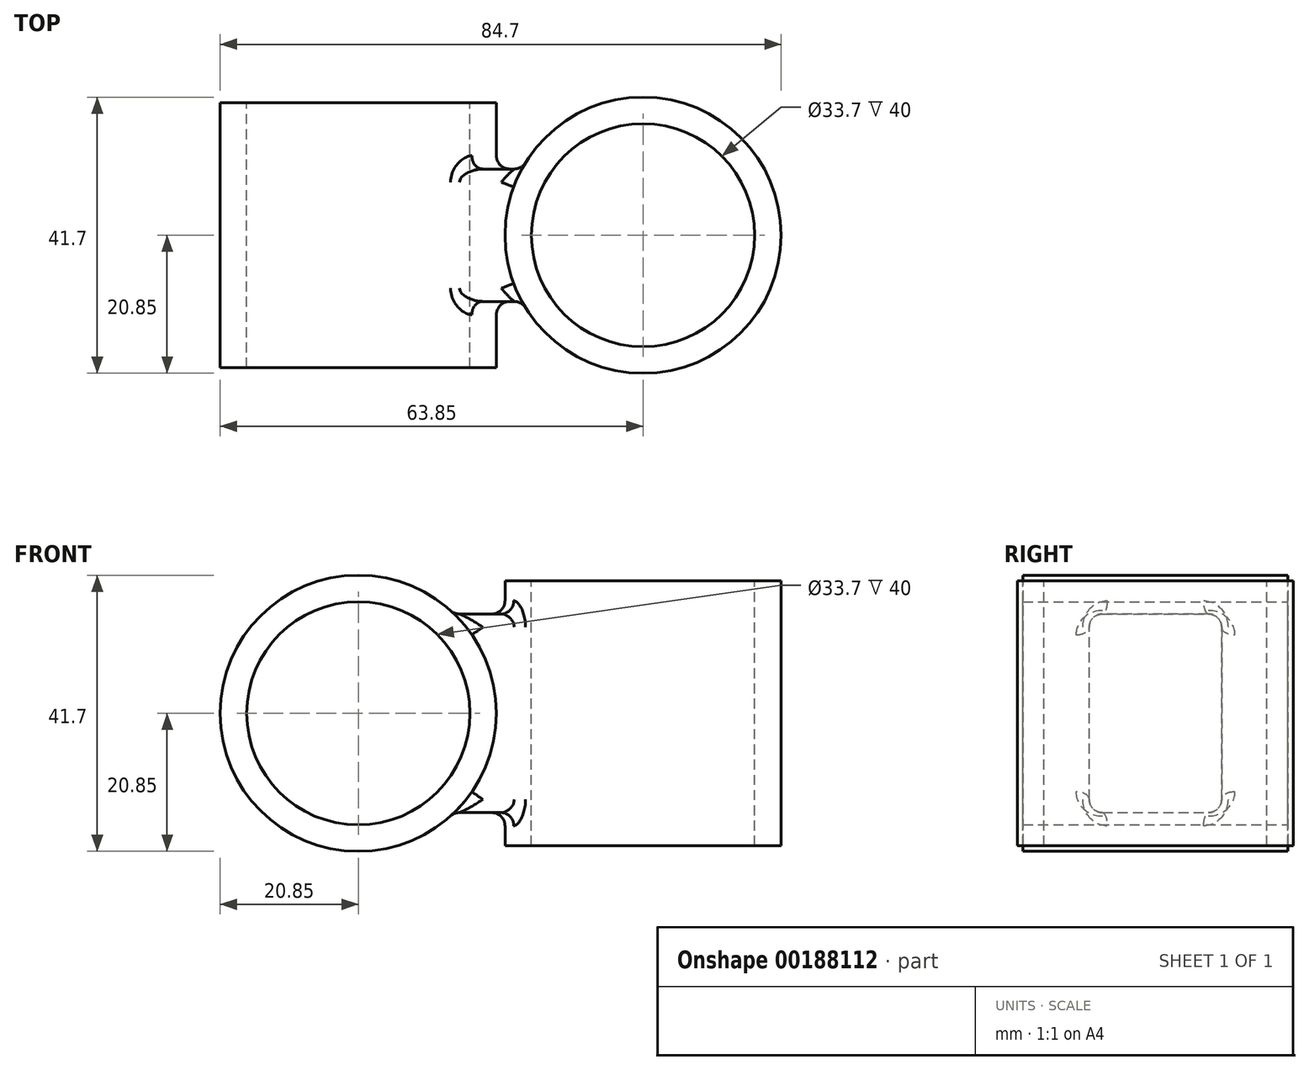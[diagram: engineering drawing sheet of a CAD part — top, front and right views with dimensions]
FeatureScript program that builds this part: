
annotation { "Feature Type Name" : "Feature", "Feature Type Description" : "" }
export const myFeature = defineFeature(function(context is Context, id is Id, definition is map)
    precondition{}
    {
        {
            var Q0;
            Q0=qCreatedBy(makeId("Front.planeOp"),FACE);
            var sketch = newSketch(context, id + "F0", { "sketchPlane" : qUnion([Q0])});
            skCircle(sketch, "E0", {"center": v(0, 0) * mm, "radius": 16.85 * mm});
            skCircle(sketch, "E1", {"center": v(0, 0) * mm, "radius": 20.85 * mm});
            skSolve(sketch);
        }
        {
            var Q0;
            Q0=makeQuery(id+"F0.imprint","IMPRINT",FACE,{"disambiguationData":[TD([[makeQuery(id+"F0.imprint","IMPRINT",EDGE,{"derivedFrom":sQuery(id+"F0.wireOp",EDGE,"E0")}),1.0]])]});
            extrude(context, id + "F1", {"entities" : qUnion([Q0]), "depth" : 40 * mm, "symmetric" : true});
        }
        {
            var Q0;
            Q0=makeQuery(id+"F0.imprint","IMPRINT",FACE,{"disambiguationData":[TD([[makeQuery(id+"F0.imprint","IMPRINT",EDGE,{"derivedFrom":sQuery(id+"F0.wireOp",EDGE,"E0")}),-1.0]])]});
            extrude(context, id + "F2", {"entities" : qUnion([Q0]), "depth" : 40 * mm, "symmetric" : true});
        }
        {
            var Q0;
            Q0=makeQuery(id+"F2.opExtrude","SWEPT_BODY",BODY,{"disambiguationData":[OSD([sQuery(id+"F0.wireOp",EDGE,"E0"),sQuery(id+"F0.wireOp",EDGE,"E1")])]});
            transform(context, id + "F3", {"entities" : qUnion([Q0]), "transformType" : TransformType.TRANSLATION_3D, "dx" : 43 * mm, "dy" : 0 * mm, "dz" : 0 * mm, "makeCopy" : true});
        }
        {
            var Q0;
            Q0=makeQuery(id+"F1.opExtrude","SWEPT_BODY",BODY,{"disambiguationData":[OSD([sQuery(id+"F0.wireOp",EDGE,"E0")])]});
            transform(context, id + "F4", {"entities" : qUnion([Q0]), "transformType" : TransformType.TRANSLATION_3D, "dx" : 43 * mm, "dy" : 0 * mm, "dz" : 0 * mm, "makeCopy" : true});
        }
        {
            var Q0;
            Q0=qCreatedBy(makeId("Front.planeOp"),FACE);
            var sketch = newSketch(context, id + "F5", { "sketchPlane" : qUnion([Q0])});
            skLineSegment(sketch, "E2.bottom", {"start": v(30.5, 15) * mm, "end": v(12.5, 15) * mm});
            skLineSegment(sketch, "E2.top", {"start": v(30.5, -15) * mm, "end": v(12.5, -15) * mm});
            skLineSegment(sketch, "E2.left", {"start": v(30.5, 15) * mm, "end": v(30.5, -15) * mm});
            skLineSegment(sketch, "E2.right", {"start": v(12.5, 15) * mm, "end": v(12.5, -15) * mm});
            skPoint(sketch, "E2.middle", {"position": v(21.5, 0) * mm});
            skLineSegment(sketch, "E3", {"start": v(14.35, 0) * mm, "end": v(26.07, 0) * mm});
            skSolve(sketch);
        }
        {
            var Q0;
            Q0=makeQuery(id+"F3.opPattern","COPY",BODY,{"derivedFrom":makeQuery(id+"F2.opExtrude","SWEPT_BODY",BODY,{"disambiguationData":[OSD([sQuery(id+"F0.wireOp",EDGE,"E0"),sQuery(id+"F0.wireOp",EDGE,"E1")])]}),"instanceName":"1"});
            var Q1;
            Q1=sQuery(id+"F5.wireOp",EDGE,"E3");
            transform(context, id + "F6", {"entities" : qUnion([Q0]), "transformType" : TransformType.ROTATION, "transformAxis" : qUnion([Q1]), "angle" : 90 * degree, "makeCopy" : false});
        }
        {
            var Q0;
            Q0=makeQuery(id+"F4.opPattern","COPY",BODY,{"derivedFrom":makeQuery(id+"F1.opExtrude","SWEPT_BODY",BODY,{"disambiguationData":[OSD([sQuery(id+"F0.wireOp",EDGE,"E0")])]}),"instanceName":"1"});
            var Q1;
            Q1=sQuery(id+"F5.wireOp",EDGE,"E3");
            transform(context, id + "F7", {"entities" : qUnion([Q0]), "transformType" : TransformType.ROTATION, "transformAxis" : qUnion([Q1]), "angle" : 90 * degree, "makeCopy" : false});
        }
        {
            var Q0;
            Q0=makeQuery(id+"F5.imprint","IMPRINT",FACE,{"disambiguationData":[TD([[makeQuery(id+"F5.imprint","IMPRINT",EDGE,{"derivedFrom":sQuery(id+"F5.wireOp",EDGE,"E2.bottom")}),1.0]])]});
            extrude(context, id + "F8", {"entities" : qUnion([Q0]), "depth" : 20 * mm, "symmetric" : true});
        }
        {
            var Q0;
            Q0=makeQuery(id+"F1.opExtrude","SWEPT_BODY",BODY,{"disambiguationData":[OSD([sQuery(id+"F0.wireOp",EDGE,"E0")])]});
            var Q1;
            Q1=makeQuery(id+"F4.opPattern","COPY",BODY,{"derivedFrom":makeQuery(id+"F1.opExtrude","SWEPT_BODY",BODY,{"disambiguationData":[OSD([sQuery(id+"F0.wireOp",EDGE,"E0")])]}),"instanceName":"1"});
            var Q2;
            Q2=makeQuery(id+"F8.opExtrude","SWEPT_BODY",BODY,{"disambiguationData":[OSD([sQuery(id+"F5.wireOp",EDGE,"E2.bottom"),sQuery(id+"F5.wireOp",EDGE,"E2.top"),sQuery(id+"F5.wireOp",EDGE,"E2.left"),sQuery(id+"F5.wireOp",EDGE,"E2.right")])]});
            booleanBodies(context, id + "F9", {"operationType" : BooleanOperationType.SUBTRACTION, "tools" : qUnion([Q0, Q1]), "targets" : qUnion([Q2])});
        }
        {
            var Q0;
            Q0=makeQuery(id+"F2.opExtrude","SWEPT_BODY",BODY,{"disambiguationData":[OSD([sQuery(id+"F0.wireOp",EDGE,"E0"),sQuery(id+"F0.wireOp",EDGE,"E1")])]});
            var Q1;
            Q1=makeQuery(id+"F8.opExtrude","SWEPT_BODY",BODY,{"disambiguationData":[OSD([sQuery(id+"F5.wireOp",EDGE,"E2.bottom"),sQuery(id+"F5.wireOp",EDGE,"E2.top"),sQuery(id+"F5.wireOp",EDGE,"E2.left"),sQuery(id+"F5.wireOp",EDGE,"E2.right")])]});
            var Q2;
            Q2=makeQuery(id+"F3.opPattern","COPY",BODY,{"derivedFrom":makeQuery(id+"F2.opExtrude","SWEPT_BODY",BODY,{"disambiguationData":[OSD([sQuery(id+"F0.wireOp",EDGE,"E0"),sQuery(id+"F0.wireOp",EDGE,"E1")])]}),"instanceName":"1"});
            booleanBodies(context, id + "F10", {"operationType" : BooleanOperationType.UNION, "tools" : qUnion([Q0, Q1, Q2])});
        }
        {
            var Q0;
            Q0=makeQuery(id+"F10.opBoolean","INTERSECT",EDGE,{"derivedFrom":[makeQuery(id+"F3.opPattern","COPY",FACE,{"derivedFrom":makeQuery(id+"F2.opExtrude","SWEPT_FACE",FACE,{"disambiguationData":[OSD([sQuery(id+"F0.wireOp",EDGE,"E1")])]}),"instanceName":"1"}),makeQuery(id+"F8.opExtrude","CAP_FACE",FACE,{"disambiguationData":[OSD([sQuery(id+"F5.wireOp",EDGE,"E2.bottom"),sQuery(id+"F5.wireOp",EDGE,"E2.top"),sQuery(id+"F5.wireOp",EDGE,"E2.left"),sQuery(id+"F5.wireOp",EDGE,"E2.right")])],"isStart":false})]});
            var Q1;
            Q1=makeQuery(id+"F8.opExtrude","CAP_FACE",FACE,{"disambiguationData":[OSD([sQuery(id+"F5.wireOp",EDGE,"E2.bottom"),sQuery(id+"F5.wireOp",EDGE,"E2.top"),sQuery(id+"F5.wireOp",EDGE,"E2.left"),sQuery(id+"F5.wireOp",EDGE,"E2.right")])],"isStart":false});
            var Q2;
            Q2=makeQuery(id+"F8.opExtrude","SWEPT_FACE",FACE,{"disambiguationData":[OSD([sQuery(id+"F5.wireOp",EDGE,"E2.top")])]});
            var Q3;
            Q3=makeQuery(id+"F8.opExtrude","CAP_FACE",FACE,{"disambiguationData":[OSD([sQuery(id+"F5.wireOp",EDGE,"E2.bottom"),sQuery(id+"F5.wireOp",EDGE,"E2.top"),sQuery(id+"F5.wireOp",EDGE,"E2.left"),sQuery(id+"F5.wireOp",EDGE,"E2.right")])],"isStart":true});
            var Q4;
            Q4=makeQuery(id+"F8.opExtrude","SWEPT_FACE",FACE,{"disambiguationData":[OSD([sQuery(id+"F5.wireOp",EDGE,"E2.bottom")])]});
            fillet(context, id + "F11", {"entities" : qUnion([Q0, Q1, Q2, Q3, Q4]), "radius" : 2 * mm, "tangentPropagation" : true, "allowEdgeOverflow" : false});
        }
    });
